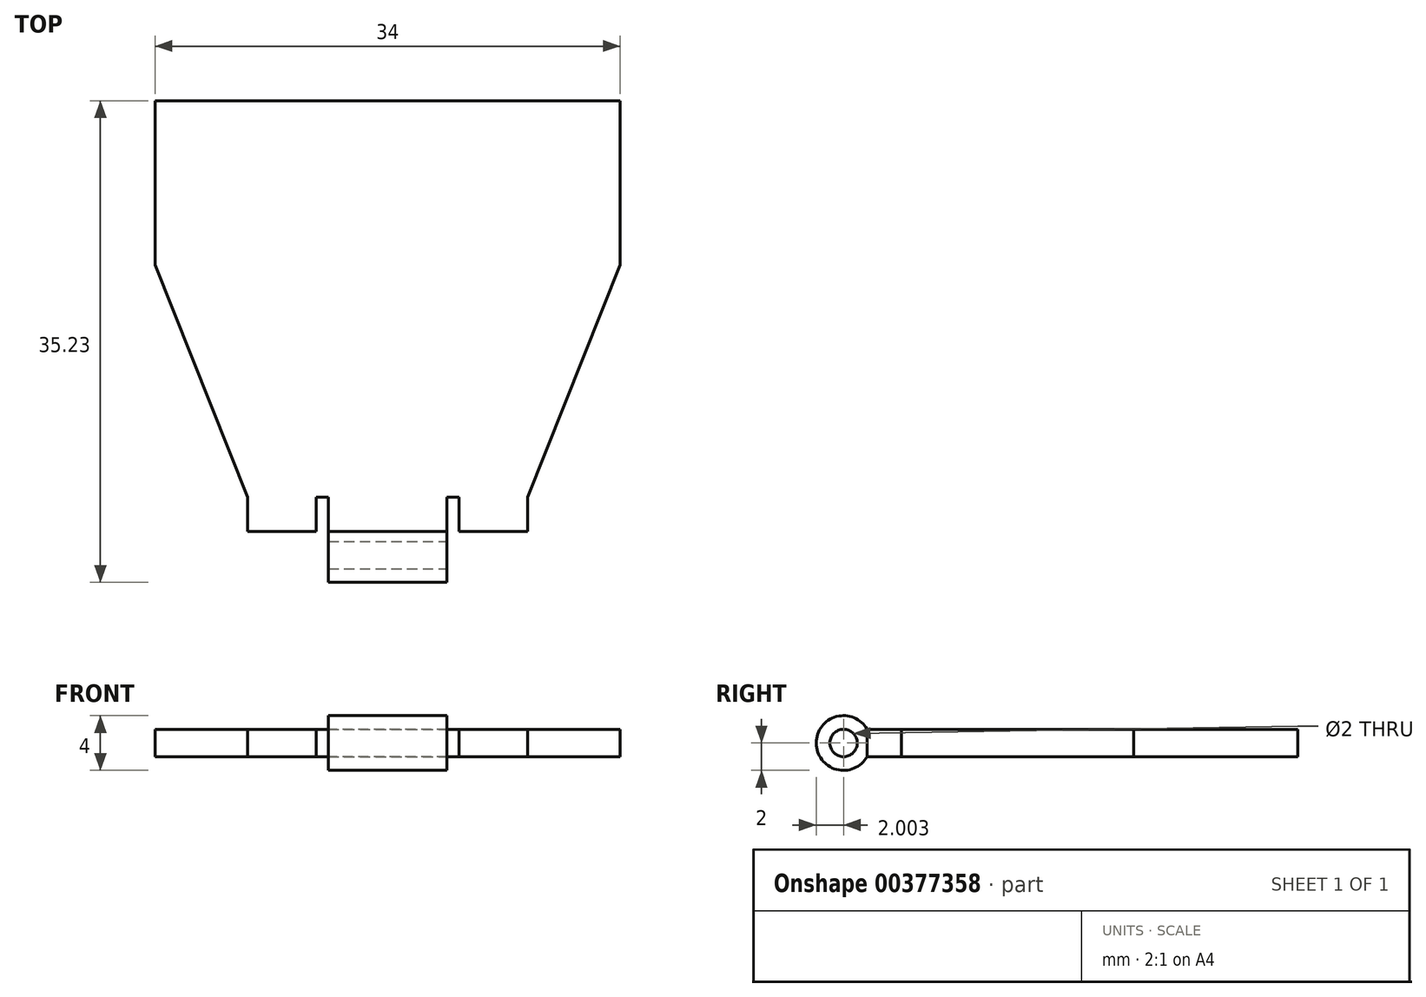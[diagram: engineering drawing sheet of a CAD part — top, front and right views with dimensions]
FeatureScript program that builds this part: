
annotation { "Feature Type Name" : "Feature", "Feature Type Description" : "" }
export const myFeature = defineFeature(function(context is Context, id is Id, definition is map)
    precondition{}
    {
        {
            var Q0;
            Q0=qCreatedBy(makeId("Top.planeOp"),FACE);
            var sketch = newSketch(context, id + "F0", { "sketchPlane" : qUnion([Q0])});
            skLineSegment(sketch, "E0.bottom", {"start": v(0, 25.5) * mm, "end": v(-10.25, 25.5) * mm});
            skLineSegment(sketch, "E0.top", {"start": v(0, 28) * mm, "end": v(-10.25, 28) * mm});
            skLineSegment(sketch, "E0.right", {"start": v(-10.25, 25.5) * mm, "end": v(-10.25, 28) * mm});
            skPoint(sketch, "E0.middle", {"position": v(0, 0) * mm});
            skLineSegment(sketch, "E1", {"start": v(-10.25, 28) * mm, "end": v(-17, 45) * mm});
            skLineSegment(sketch, "E2", {"start": v(-17, 45) * mm, "end": v(0, 45) * mm});
            skLineSegment(sketch, "E3.top", {"start": v(-17, 57) * mm, "end": v(0, 57) * mm});
            skLineSegment(sketch, "E3.left", {"start": v(-17, 45) * mm, "end": v(-17, 57) * mm});
            skLineSegment(sketch, "E4", {"start": v(0, 57) * mm, "end": v(0, 25.5) * mm, "construction": true});
            skLineSegment(sketch, "E5.MirrorCS", {"start": v(17, 57) * mm, "end": v(0, 57) * mm});
            skLineSegment(sketch, "E6.MirrorCS", {"start": v(17, 45) * mm, "end": v(17, 57) * mm});
            skLineSegment(sketch, "E7.MirrorCS", {"start": v(17, 45) * mm, "end": v(0, 45) * mm});
            skLineSegment(sketch, "E8.MirrorCS", {"start": v(10.25, 28) * mm, "end": v(17, 45) * mm});
            skLineSegment(sketch, "E9.MirrorCS", {"start": v(0, 28) * mm, "end": v(10.25, 28) * mm});
            skLineSegment(sketch, "E10.MirrorCS", {"start": v(10.25, 25.5) * mm, "end": v(10.25, 28) * mm});
            skLineSegment(sketch, "E11.MirrorCS", {"start": v(0, 25.5) * mm, "end": v(10.25, 25.5) * mm});
            skSolve(sketch);
        }
        {
            var Q0;
            Q0=qSketchRegion(id+"F0",true);
            extrude(context, id + "F1", {"entities" : qUnion([Q0]), "depth" : 2 * mm});
        }
        {
            var Q0;
            Q0=qCreatedBy(makeId("Right.planeOp"),FACE);
            var sketch = newSketch(context, id + "F2", { "sketchPlane" : qUnion([Q0])});
            skCircle(sketch, "E12", {"center": v(23.77, 1) * mm, "radius": 1 * mm});
            skCircle(sketch, "E13.0", {"center": v(23.77, 1) * mm, "radius": 2 * mm});
            skSolve(sketch);
        }
        {
            var Q0;
            Q0=makeQuery(id+"F2.imprint","IMPRINT",FACE,{"disambiguationData":[TD([[makeQuery(id+"F2.imprint","IMPRINT",EDGE,{"derivedFrom":sQuery(id+"F2.wireOp",EDGE,"E12")}),-1.0]])]});
            var Q1;
            Q1=makeQuery(id+"F1.opExtrude","SWEPT_FACE",FACE,{"disambiguationData":[OSD([sQuery(id+"F0.wireOp",EDGE,"E0.right")])]});
            extrude(context, id + "F3", {"entities" : qUnion([Q0]), "operationType" : NewBodyOperationType.ADD, "oppositeDirection" : true, "endBoundEntityFace" : qUnion([Q1]), "depth" : (8.65 / 2) * mm, "hasSecondDirection" : true, "secondDirectionOppositeDirection" : false, "secondDirectionDepth" : (8.65 / 2) * mm});
        }
        {
            var Q0;
            Q0=makeQuery(id+"Fh0vniOlRHHV3WY_2.boolean.opBoolean","MERGE",FACE,{"derivedFrom":[makeQuery(id+"F1.opExtrude","CAP_FACE",FACE,{"disambiguationData":[OSD([sQuery(id+"F0.wireOp",EDGE,"E0.bottom"),sQuery(id+"F0.wireOp",EDGE,"E0.right"),sQuery(id+"F0.wireOp",EDGE,"E1"),sQuery(id+"F0.wireOp",EDGE,"E3.top"),sQuery(id+"F0.wireOp",EDGE,"E3.left"),sQuery(id+"F0.wireOp",EDGE,"E5.MirrorCS"),sQuery(id+"F0.wireOp",EDGE,"E6.MirrorCS"),sQuery(id+"F0.wireOp",EDGE,"E8.MirrorCS"),sQuery(id+"F0.wireOp",EDGE,"E10.MirrorCS"),sQuery(id+"F0.wireOp",EDGE,"E11.MirrorCS")])],"isStart":false}),makeQuery(id+"Fh0vniOlRHHV3WY_2.opExtrude","SWEPT_FACE",FACE,{"disambiguationData":[OSD([sQuery(id+"FiDzJ6BEypaCOpJ_2.wireOp",EDGE,"XspTkoiv-8v0d-nWq4-S3MJ-6wGyW78Kte7R.bottom")])]})]});
            var sketch = newSketch(context, id + "F4", { "sketchPlane" : qUnion([Q0])});
            skLineSegment(sketch, "E14.bottom", {"start": v(4.33, 25.5) * mm, "end": v(5.22, 25.5) * mm});
            skLineSegment(sketch, "E14.top", {"start": v(4.33, 28) * mm, "end": v(5.22, 28) * mm});
            skLineSegment(sketch, "E14.left", {"start": v(4.33, 25.5) * mm, "end": v(4.33, 28) * mm});
            skLineSegment(sketch, "E14.right", {"start": v(5.22, 25.5) * mm, "end": v(5.22, 28) * mm});
            skLineSegment(sketch, "E15.MirrorCS", {"start": v(-4.33, 25.5) * mm, "end": v(-5.22, 25.5) * mm});
            skLineSegment(sketch, "E16.MirrorCS", {"start": v(-5.22, 25.5) * mm, "end": v(-5.22, 28) * mm});
            skLineSegment(sketch, "E17.MirrorCS", {"start": v(-4.33, 25.5) * mm, "end": v(-4.33, 28) * mm});
            skLineSegment(sketch, "E18.MirrorCS", {"start": v(-4.33, 28) * mm, "end": v(-5.22, 28) * mm});
            skSolve(sketch);
        }
        {
            var Q0;
            Q0 = qSketchRegion(id + "F4", true);
            extrude(context, id + "F5", {"entities" : qUnion([Q0]), "operationType" : NewBodyOperationType.REMOVE, "endBound" : BoundingType.THROUGH_ALL, "oppositeDirection" : true, "depth" : 25 * mm});
        }
    });
